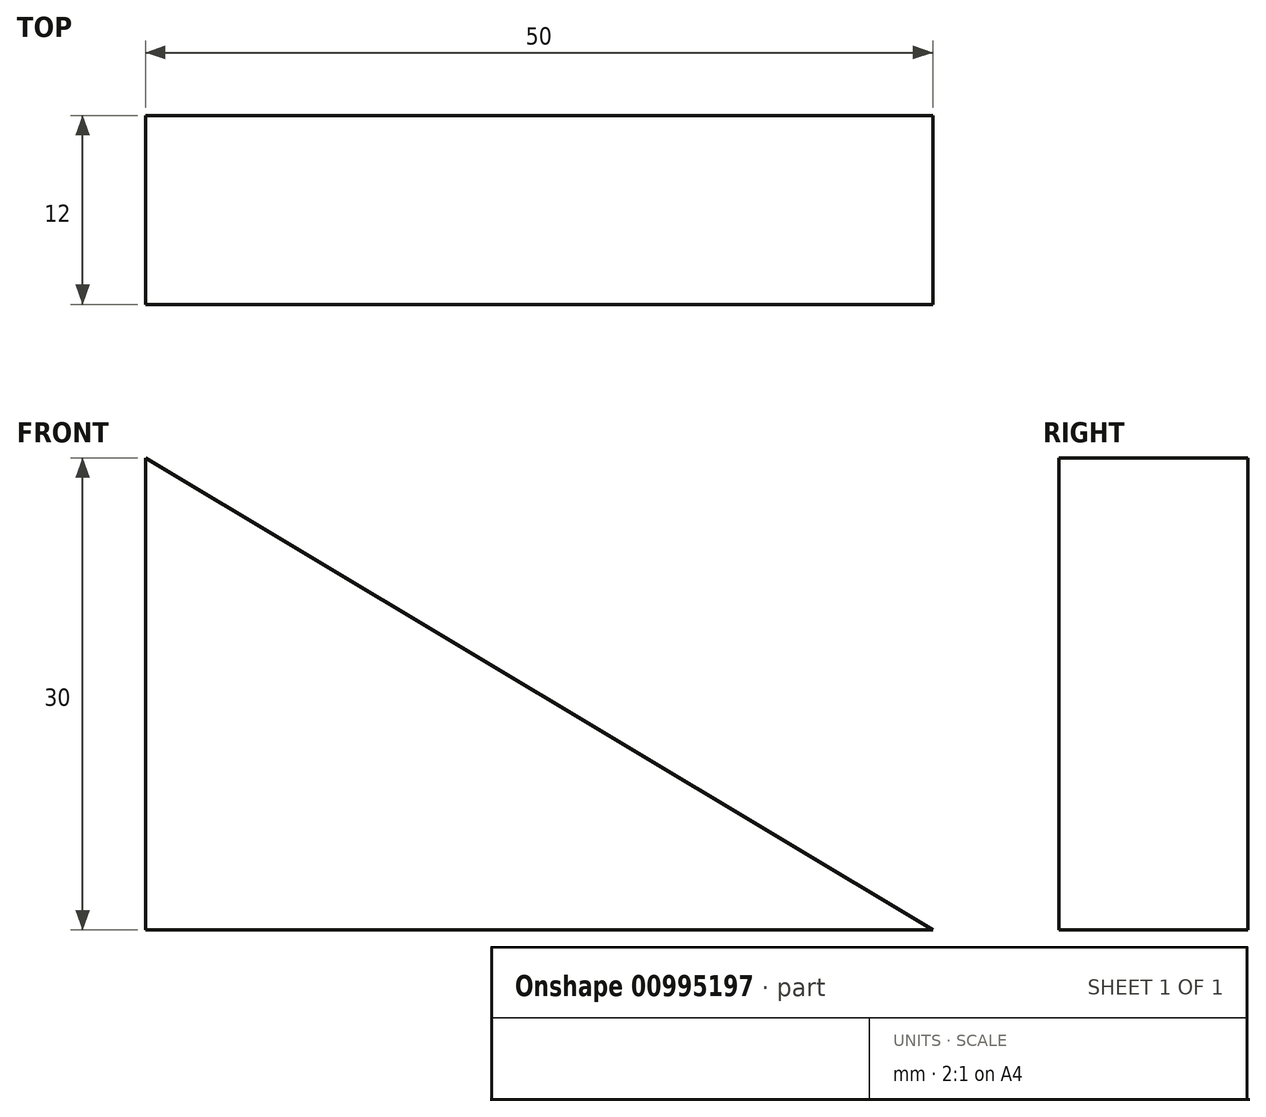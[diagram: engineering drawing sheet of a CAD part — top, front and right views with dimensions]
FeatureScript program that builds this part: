
annotation { "Feature Type Name" : "Feature", "Feature Type Description" : "" }
export const myFeature = defineFeature(function(context is Context, id is Id, definition is map)
    precondition{}
    {
        {
            var Q0;
            Q0=qCreatedBy(makeId("Front.planeOp"),FACE);
            var sketch = newSketch(context, id + "F0", { "sketchPlane" : qUnion([Q0])});
            skLineSegment(sketch, "E0", {"start": v(0, 0) * mm, "end": v(0, 30) * mm});
            skLineSegment(sketch, "E1", {"start": v(0, 30) * mm, "end": v(50, 0) * mm});
            skLineSegment(sketch, "E2", {"start": v(50, 0) * mm, "end": v(0, 0) * mm});
            skSolve(sketch);
        }
        {
            var Q0;
            Q0=makeQuery(id+"F0.imprint","IMPRINT",FACE,{"disambiguationData":[TD([[makeQuery(id+"F0.imprint","IMPRINT",EDGE,{"derivedFrom":sQuery(id+"F0.wireOp",EDGE,"E0")}),-1.0]])]});
            extrude(context, id + "F1", {"entities" : qUnion([Q0]), "oppositeDirection" : true, "depth" : 12 * mm, "offsetDistance" : 25 * mm});
        }
    });
